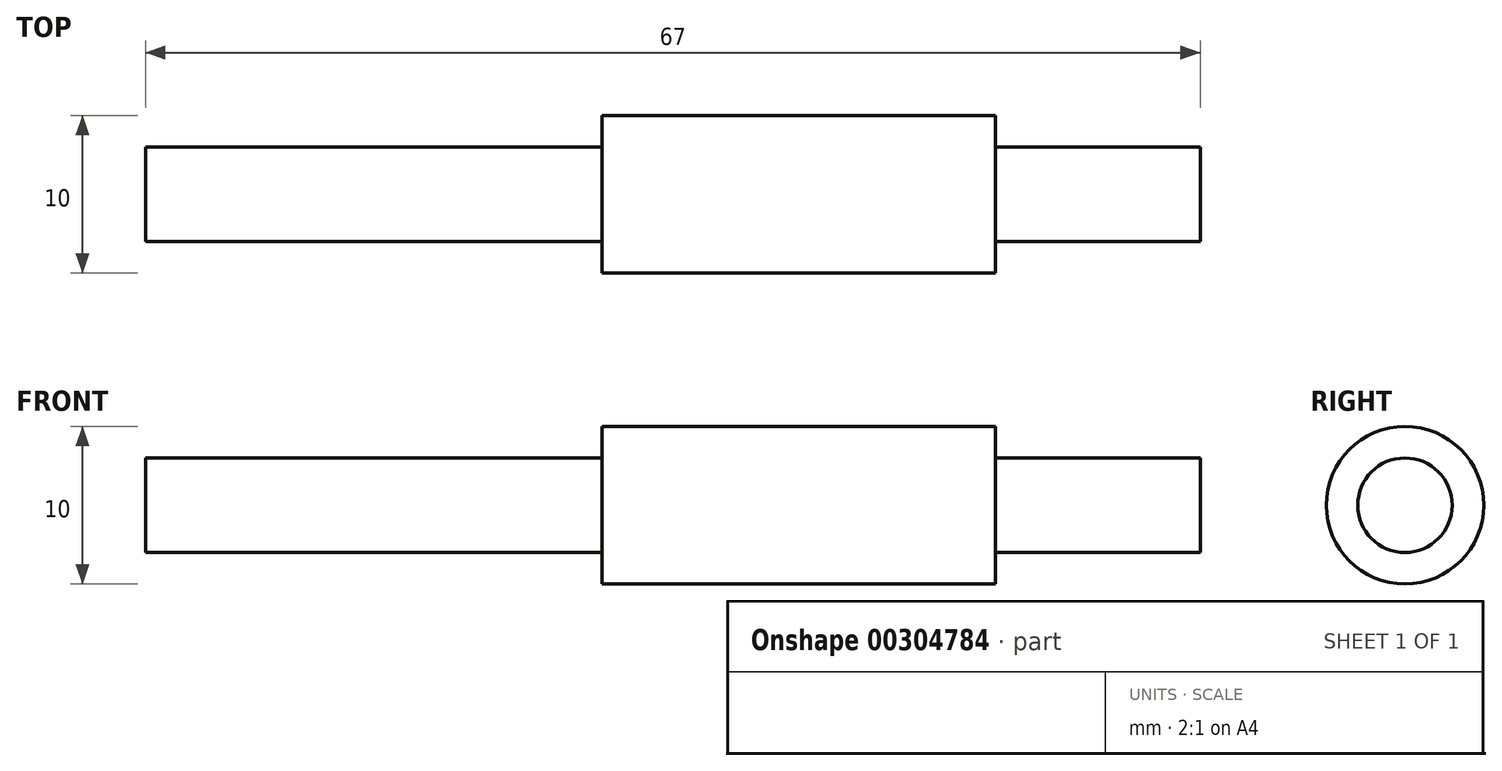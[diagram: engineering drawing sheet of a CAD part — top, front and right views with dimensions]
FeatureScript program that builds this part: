
annotation { "Feature Type Name" : "Feature", "Feature Type Description" : "" }
export const myFeature = defineFeature(function(context is Context, id is Id, definition is map)
    precondition{}
    {
        {
            var Q0;
            Q0=qCreatedBy(makeId("Front.planeOp"),FACE);
            var sketch = newSketch(context, id + "F0", { "sketchPlane" : qUnion([Q0])});
            skLineSegment(sketch, "E0.bottom", {"start": v(0, 5) * mm, "end": v(25, 5) * mm});
            skLineSegment(sketch, "E0.left", {"start": v(0, 5) * mm, "end": v(0, 0) * mm});
            skLineSegment(sketch, "E0.right", {"start": v(25, 5) * mm, "end": v(25, 0) * mm});
            skLineSegment(sketch, "E1.bottom", {"start": v(0, 3) * mm, "end": v(-23, 3) * mm});
            skLineSegment(sketch, "E1.left", {"start": v(0, 3) * mm, "end": v(0, 0) * mm});
            skLineSegment(sketch, "E1.right", {"start": v(-23, 3) * mm, "end": v(-23, 0) * mm});
            skLineSegment(sketch, "E2.top", {"start": v(-23, 3) * mm, "end": v(-29, 3) * mm});
            skLineSegment(sketch, "E2.left", {"start": v(-23, 0) * mm, "end": v(-23, 3) * mm});
            skLineSegment(sketch, "E2.right", {"start": v(-29, 0) * mm, "end": v(-29, 3) * mm});
            skPoint(sketch, "E3.positionSnap0", {"position": v(25, 0) * mm});
            skPoint(sketch, "E4", {"position": v(-23, 0) * mm});
            skLineSegment(sketch, "E5", {"start": v(-23, 0) * mm, "end": v(25, 0) * mm});
            skPoint(sketch, "E6", {"position": v(-29, 0) * mm});
            skPoint(sketch, "E7.orphan", {"position": v(-23, -3) * mm});
            skLineSegment(sketch, "E8", {"start": v(-29, 0) * mm, "end": v(-23, 0) * mm});
            skLineSegment(sketch, "E9.bottom", {"start": v(25, 0) * mm, "end": v(38, 0) * mm});
            skLineSegment(sketch, "E9.top", {"start": v(25, 3) * mm, "end": v(38, 3) * mm});
            skLineSegment(sketch, "E9.left", {"start": v(25, 0) * mm, "end": v(25, 3) * mm});
            skLineSegment(sketch, "E9.right", {"start": v(38, 0) * mm, "end": v(38, 3) * mm});
            skSolve(sketch);
        }
        {
            var Q0;
            {var subQ6=sQuery(id+"F0.wireOp",EDGE,"E0.top");Q0=makeQuery(id+"F0.imprint","IMPRINT",FACE,{"disambiguationData":[TD([[makeQuery(id+"F0.imprint","IMPRINT",EDGE,{"derivedFrom":subQ6}),1.0]])]});}
            var Q1;
            {var subQ6=sQuery(id+"F0.wireOp",EDGE,"E0.bottom");Q1=makeQuery(id+"F0.imprint","IMPRINT",FACE,{"disambiguationData":[TD([[makeQuery(id+"F0.imprint","IMPRINT",EDGE,{"derivedFrom":subQ6}),-1.0]])]});}
            var Q2;
            {var subQ0=sQuery(id+"F0.wireOp",EDGE,"E1.bottom");Q2=makeQuery(id+"F0.imprint","IMPRINT",FACE,{"disambiguationData":[TD([[makeQuery(id+"F0.imprint","IMPRINT",EDGE,{"derivedFrom":subQ0}),1.0]])]});}
            var Q3;
            {var subQ0=sQuery(id+"F0.wireOp",EDGE,"E1.top");Q3=makeQuery(id+"F0.imprint","IMPRINT",FACE,{"disambiguationData":[TD([[makeQuery(id+"F0.imprint","IMPRINT",EDGE,{"derivedFrom":subQ0}),-1.0]])]});}
            var Q4;
            {var subQ3=sQuery(id+"F0.wireOp",EDGE,"E2.bottom");Q4=makeQuery(id+"F0.imprint","IMPRINT",FACE,{"disambiguationData":[TD([[makeQuery(id+"F0.imprint","IMPRINT",EDGE,{"derivedFrom":subQ3}),-1.0]])]});}
            var Q5;
            Q5=makeQuery(id+"F0.imprint","IMPRINT",FACE,{"disambiguationData":[TD([[makeQuery(id+"F0.imprint","IMPRINT",EDGE,{"derivedFrom":sQuery(id+"F0.wireOp",EDGE,"E2.top")}),1.0]])]});
            var Q6;
            Q6=makeQuery(id+"F0.imprint","IMPRINT",FACE,{"disambiguationData":[TD([[makeQuery(id+"F0.imprint","IMPRINT",EDGE,{"derivedFrom":sQuery(id+"F0.wireOp",EDGE,"E9.bottom")}),1.0]])]});
            var Q7;
            Q7=sQuery(id+"F0.wireOp",EDGE,"E5");
            var Q8;
            Q8=sQuery(id+"F0.wireOp",EDGE,"E5");
            revolve(context, id + "F1", {"surfaceOperationType" : NewSurfaceOperationType.NEW, "entities" : qUnion([Q0, Q1, Q2, Q3, Q4, Q5, Q6]), "surfaceEntities" : qUnion([Q7]), "axis" : qUnion([Q8]), "revolveType" : RevolveType.FULL});
        }
    });
